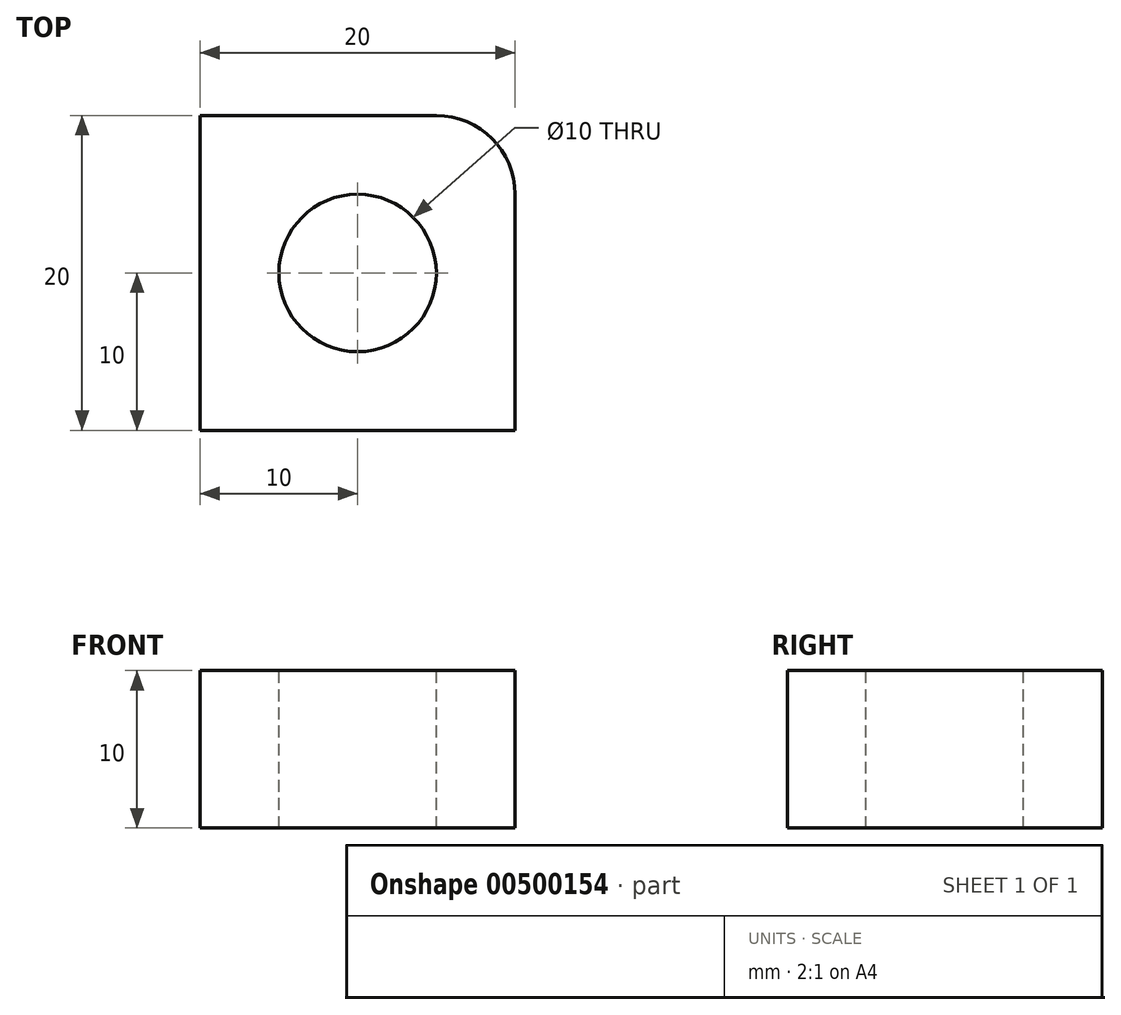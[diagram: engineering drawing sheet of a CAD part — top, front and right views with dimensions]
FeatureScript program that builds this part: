
annotation { "Feature Type Name" : "Feature", "Feature Type Description" : "" }
export const myFeature = defineFeature(function(context is Context, id is Id, definition is map)
    precondition{}
    {
        {
            var Q0;
            Q0=qCreatedBy(makeId("Top.planeOp"),FACE);
            var sketch = newSketch(context, id + "F0", { "sketchPlane" : qUnion([Q0])});
            skLineSegment(sketch, "E0.bottom", {"start": v(10, -10) * mm, "end": v(-10, -10) * mm});
            skLineSegment(sketch, "E0.top", {"start": v(10, 10) * mm, "end": v(-10, 10) * mm});
            skLineSegment(sketch, "E0.left", {"start": v(10, -10) * mm, "end": v(10, 10) * mm});
            skLineSegment(sketch, "E0.right", {"start": v(-10, -10) * mm, "end": v(-10, 10) * mm});
            skPoint(sketch, "E0.middle", {"position": v(0, 0) * mm});
            skSolve(sketch);
        }
        {
            var Q0;
            Q0 = qSketchRegion(id + "F0", true);
            var Q1;
            Q1=makeQuery(id+"F0.imprint","IMPRINT",FACE,{"disambiguationData":[TD([[makeQuery(id+"F0.imprint","IMPRINT",EDGE,{"derivedFrom":sQuery(id+"F0.wireOp",EDGE,"E0.bottom")}),-1.0]])]});
            extrude(context, id + "F1", {"entities" : qUnion([Q0, Q1]), "depth" : 10 * mm});
        }
        {
            var Q0;
            Q0=makeQuery(id+"F1.opExtrude","CAP_FACE",FACE,{"disambiguationData":[OSD([sQuery(id+"F0.wireOp",EDGE,"E0.bottom"),sQuery(id+"F0.wireOp",EDGE,"E0.top"),sQuery(id+"F0.wireOp",EDGE,"E0.left"),sQuery(id+"F0.wireOp",EDGE,"E0.right")])],"isStart":false});
            var sketch = newSketch(context, id + "F2", { "sketchPlane" : qUnion([Q0])});
            skPoint(sketch, "E1", {"position": v(0, 0) * mm});
            skSolve(sketch);
        }
        {
            var Q0;
            Q0=sQuery(id+"F2.wireOp",VERTEX,"E1");
            var Q1;
            Q1=makeQuery(id+"F1.opExtrude","SWEPT_BODY",BODY,{"disambiguationData":[OSD([sQuery(id+"F0.wireOp",EDGE,"E0.bottom"),sQuery(id+"F0.wireOp",EDGE,"E0.top"),sQuery(id+"F0.wireOp",EDGE,"E0.left"),sQuery(id+"F0.wireOp",EDGE,"E0.right")])]});
            hole(context, id + "F3", {"style" : HoleStyle.SIMPLE, "endStyle" : HoleEndStyle.THROUGH, "holeDiameter" : 10 * mm, "isTappedThrough" : true, "tappedDepth" : 12 * mm, "tapClearance" : 3, "locations" : qUnion([Q0]), "scope" : qUnion([Q1])});
        }
        {
            var Q0;
            Q0=makeQuery(id+"F1.opExtrude","SWEPT_EDGE",EDGE,{"disambiguationData":[OSD([sQuery(id+"F0.wireOp",EDGE,"E0.top"),sQuery(id+"F0.wireOp",EDGE,"E0.left")])]});
            fillet(context, id + "F4", {"entities" : qUnion([Q0]), "radius" : 5 * mm, "tangentPropagation" : true, "allowEdgeOverflow" : false});
        }
    });
